# Revit family: DIK - COMPONENTI_fam
name_source: partatom
category: Generic Models
units: mm (PartAtom-declared; Revit-internal decimal feet)

## family parameters
Always vertical = Yes
Can host rebar = No
Cut with Voids When Loaded = No
Maintain Annotation Orientation = No
Part Type = Normal
Room Calculation Point = No
Round Connector Dimension = Use Diameter
Shared = No
Work Plane-Based = No

## types (2) — shared parameters
zero-valued in all types: Default Elevation

## per-type parameters (varying)
| type | ALTEZZA | LATO 1 | LATO 2 |
| 20 x 20 x 50 | 50000 mm  [stored 164.042 ft] | 20000 mm  [stored 65.6168 ft] | 20000 mm  [stored 65.6168 ft] |
| 15 x 15 x 100 | 100000 mm  [stored 328.084 ft] | 15000 mm  [stored 49.2126 ft] | 15000 mm  [stored 49.2126 ft] |

note: [stored X ft] marks values corroborated as IEEE doubles in the binary element streams (Revit-internal decimal feet)

## geometry (parser evidence)
native form markers: Sweep x3
no freeform markers — native parametric forms only
